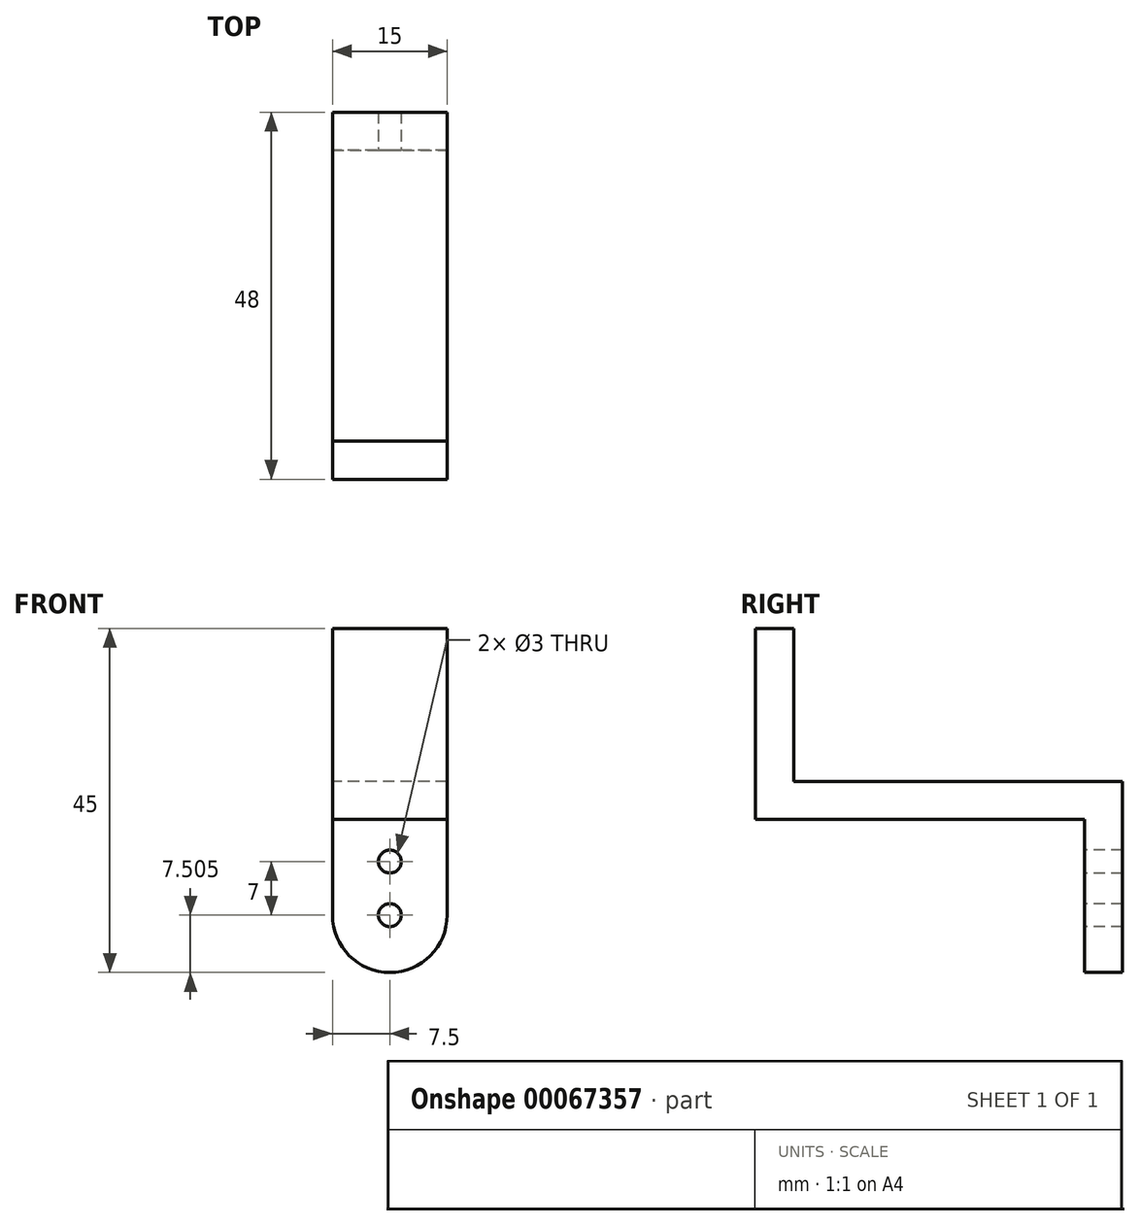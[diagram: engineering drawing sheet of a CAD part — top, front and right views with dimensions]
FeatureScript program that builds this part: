
annotation { "Feature Type Name" : "Feature", "Feature Type Description" : "" }
export const myFeature = defineFeature(function(context is Context, id is Id, definition is map)
    precondition{}
    {
        {
            var Q0;
            Q0=qCreatedBy(makeId("Right.planeOp"),FACE);
            var sketch = newSketch(context, id + "F0", { "sketchPlane" : qUnion([Q0])});
            skLineSegment(sketch, "E0", {"start": v(-24.13, 2.28) * mm, "end": v(-24.13, -17.72) * mm});
            skLineSegment(sketch, "E1", {"start": v(-24.13, -17.72) * mm, "end": v(18.87, -17.72) * mm});
            skLineSegment(sketch, "E2", {"start": v(18.87, -17.72) * mm, "end": v(18.87, -42.72) * mm});
            skLineSegment(sketch, "E3", {"start": v(18.87, -42.72) * mm, "end": v(13.87, -42.72) * mm});
            skLineSegment(sketch, "E4", {"start": v(13.87, -42.72) * mm, "end": v(13.87, -22.72) * mm});
            skLineSegment(sketch, "E5", {"start": v(13.87, -22.72) * mm, "end": v(-29.13, -22.72) * mm});
            skLineSegment(sketch, "E6", {"start": v(-29.13, -22.72) * mm, "end": v(-29.13, 2.28) * mm});
            skLineSegment(sketch, "E7", {"start": v(-29.13, 2.28) * mm, "end": v(-24.13, 2.28) * mm});
            skLineSegment(sketch, "E8", {"start": v(-24.13, -17.72) * mm, "end": v(-29.13, -17.72) * mm, "construction": true});
            skLineSegment(sketch, "E9", {"start": v(-24.13, -17.72) * mm, "end": v(-24.13, -22.72) * mm, "construction": true});
            skLineSegment(sketch, "E10", {"start": v(13.87, -22.72) * mm, "end": v(13.87, -17.72) * mm, "construction": true});
            skLineSegment(sketch, "E11", {"start": v(13.87, -22.72) * mm, "end": v(18.87, -22.72) * mm, "construction": true});
            skSolve(sketch);
        }
        {
            var Q0;
            Q0=makeQuery(id+"F0.imprint","IMPRINT",FACE,{"disambiguationData":[TD([[makeQuery(id+"F0.imprint","IMPRINT",EDGE,{"derivedFrom":sQuery(id+"F0.wireOp",EDGE,"E0")}),-1.0]])]});
            extrude(context, id + "F1", {"entities" : qUnion([Q0]), "depth" : 15 * mm});
        }
        {
            var Q0;
            Q0=makeQuery(id+"F1.opExtrude","SWEPT_FACE",FACE,{"disambiguationData":[OSD([sQuery(id+"F0.wireOp",EDGE,"E4")])]});
            var sketch = newSketch(context, id + "F2", { "sketchPlane" : qUnion([Q0])});
            skLineSegment(sketch, "E12", {"start": v(7.5, -42.72) * mm, "end": v(7.5, -22.72) * mm, "construction": true});
            skArc(sketch, "E13", {"start": v(0, -35.22) * mm, "mid": v(7.5, -42.72) * mm, "end": v(15, -35.22) * mm});
            skCircle(sketch, "E14", {"center": v(7.5, -35.22) * mm, "radius": 1.5 * mm});
            skLineSegment(sketch, "E15", {"start": v(15, -35.22) * mm, "end": v(0, -35.22) * mm, "construction": true});
            skLineSegment(sketch, "E16", {"start": v(0, -35.22) * mm, "end": v(0, -42.72) * mm});
            skLineSegment(sketch, "E17", {"start": v(0, -42.72) * mm, "end": v(15, -42.72) * mm});
            skLineSegment(sketch, "E18", {"start": v(15, -42.72) * mm, "end": v(15, -35.22) * mm});
            skCircle(sketch, "E19", {"center": v(7.5, -28.22) * mm, "radius": 1.5 * mm});
            skSolve(sketch);
        }
        {
            var Q0;
            Q0 = qSketchRegion(id + "F2", true);
            extrude(context, id + "F3", {"entities" : qUnion([Q0]), "operationType" : NewBodyOperationType.REMOVE, "endBound" : BoundingType.THROUGH_ALL, "oppositeDirection" : true, "depth" : 25 * mm});
        }
    });
